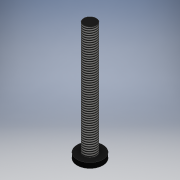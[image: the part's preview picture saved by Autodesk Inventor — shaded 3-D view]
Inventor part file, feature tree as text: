
AUTODESK INVENTOR PART (.ipt)
format: ipt  version: 2016 (Build 200138000, 138)  size: 119,808 bytes
history: native  units: mm
features: extrude x3, sketch x3, thread x1
ambient origin geometry x8: Origin, YZ Plane, XZ Plane, XY Plane, X Axis, Y Axis, Z Axis, Center Point
bodies: 实体1 (feature_tree)
feature tree (7):
  extrude  "拉伸1"  Depth=44.0mm TaperAngle=0.0deg
  extrude  "拉伸2"  Depth=2.0mm TaperAngle=0.0deg
  extrude  "拉伸3"  Depth=2.0mm TaperAngle=0.0deg
  thread  "螺纹1"  [1 undecoded]
  sketch  "草图1"  dims[d0=5.0mm d1=44.0mm d2=0.0mm]
  sketch  "草图2"  dims[d3=10.0mm d4=2.0mm d5=0.0mm]
  sketch  "草图3"  dims[d6=4.330127mm d7=2.0mm d8=0.0mm d9=10.0mm d10=0.0mm]
note: 1 required parameter value undecoded (feature->parameter linkage not recoverable at this tier; creation-order binding heuristic only, values carry confidence <= 0.55)
